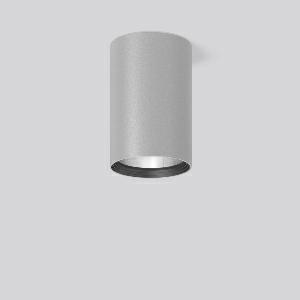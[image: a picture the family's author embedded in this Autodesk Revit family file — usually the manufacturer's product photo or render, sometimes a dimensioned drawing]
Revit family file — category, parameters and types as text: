
# Revit family: heledon_maxi_a_931223_004_3_76_48ef
name_source: partatom
category: Lighting Fixtures
units: mm (PartAtom-declared; Revit-internal decimal feet)

## family parameters
Cut with Voids When Loaded = No
Host = Face
Light Source = No
Part Type = Normal
Room Calculation Point = No
Round Connector Dimension = Use Diameter
Shared = No

## types (1)
- HELEDON maxi A (1 x LED Modul 935, 4250 lm, 3500)
    Apparent Load = 35 VA
    Approval mark = CE
    CIE Flux Codes = 100 100 100 100 100
    Color Rendering = 92
    Color Temperature = 3500
    Default Elevation = 1800 mm
    Description = Series: HELEDON maxi
Cylindrical surface-mounted downlight. Housing: die-cast aluminium, powder-coated. Internal ceiling frame polycarbonate with bayonet mounting. Black plastic ring and recessed LED to prevent glare from the side. Optical assembly with reflector made of MIRO-Silver with 98% total light reflection for outstanding efficiency - can be changed without tools. Best colour rendering index Ra>90. Suitable for Ceiling mounting. Easy installation with a separate ceiling frame with bayonet mounting and plug connection. Driver integrated. Connected via plug-in connector. High quality converter without flickering and stroboscopic effect. The following accessories can be mounted without use of tools: interchangeable lenses, decorative glasses, honeycomb louvre, clear and frosted diffusers, white interchangeable plastic ring. 
Colour: silver
Diameter: 123 mm
Height: 183 mm
Lamp: LED
Socket: without socket
Colour temperature: 3500K
Colour rendering index (CRI): 92
System power: 35 W
Rated luminous flux: 4250 lm
Luminous efficiency: 121 lm/W
Control gear: Converter, dimmable, DALI
Protection class: I
Type of protection: IP 20
    Height = 183 mm
    Lamp = 1 x LED Modul 935
    Lamp Light Flux = 4250 lm
    Lamp count = 1
    Length = 123 mm
    Lifetime = 50000 h
    Luminous efficacy = 121 lm/W
    Manufacturer = RZB
    ModVariant = No
    Model = 931223.004.3.76
    Mounting Place = Ceiling
    Mounting Type = Surface mounted
    Number of Poles = 1
    OnlyDefault = Yes
    Power Factor = 1
    Product Name = HELEDON maxi A
    Product group = Surface mounted downlights
    ProductGroupID = 302
    Protection Class = Protection class I
    Protection Degree = IP 20
    RLX_Detail_Level = 1
    RLX_Emergency_Light_Flux = 0 lm
    RLX_Emergency_Type = 0
    RLX_Emergency_Type_DB = No
    RlxData = <blob elided: 98517 chars, md5=4018003f>
    Socket = socket
    Standby Power = 0 W
    System Light Flux = 4250 lm
    System Power = 35 W
    Type Comments = Product without accessories
    Type Image = 931192.004.jpg
    URL = http://relux.com
    VarID = ---
    Voltage = 230 V
    Voltage Range = 220-240 V
    Weight = 0.00 kg
    Width = 0 mm  [stored 0 ft]

note: [stored X ft] marks values corroborated as IEEE doubles in the binary element streams (Revit-internal decimal feet)

## geometry (parser evidence)
native form markers: Blend x4, Sweep x10
no freeform markers — native parametric forms only
